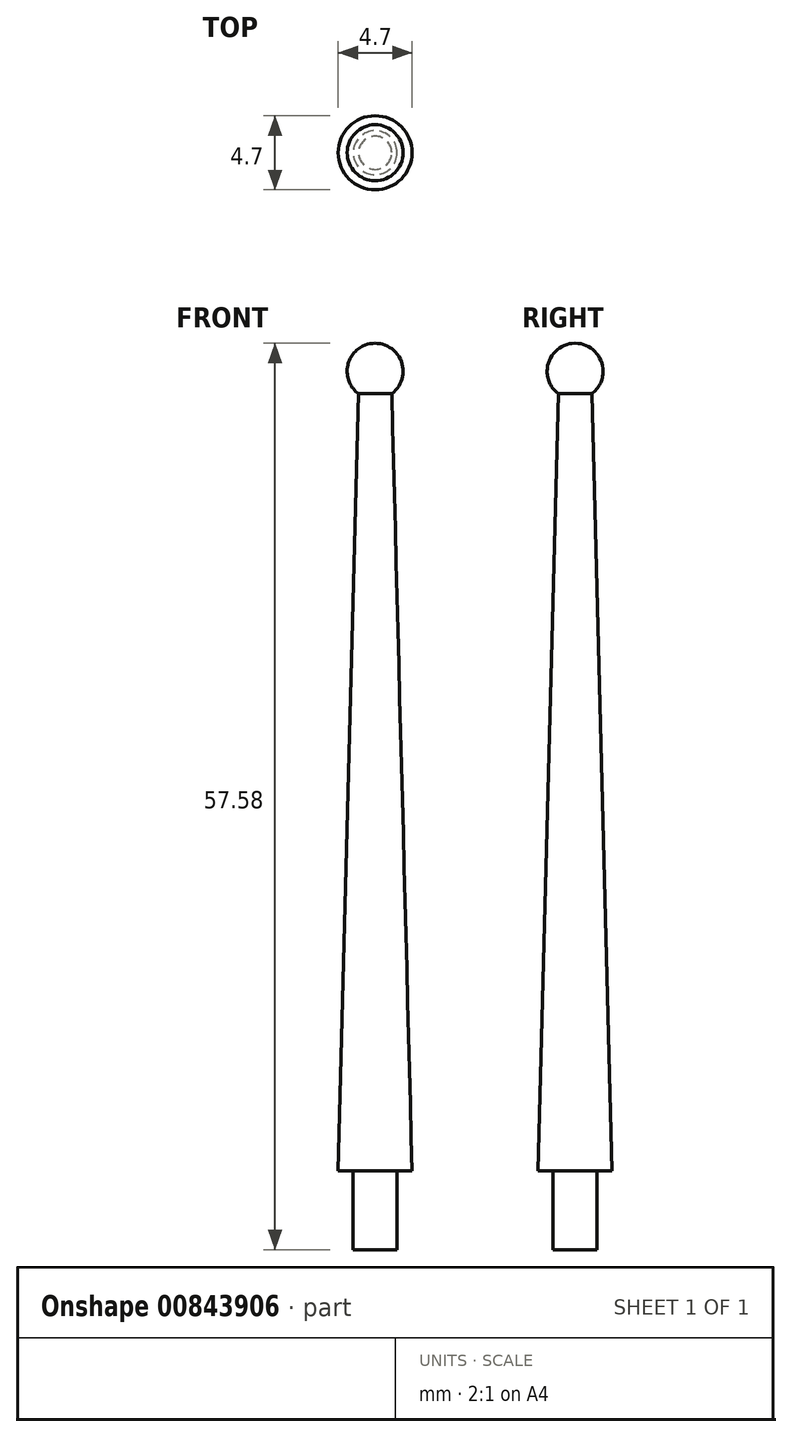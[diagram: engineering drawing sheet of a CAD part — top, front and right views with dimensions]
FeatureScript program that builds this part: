
annotation { "Feature Type Name" : "Feature", "Feature Type Description" : "" }
export const myFeature = defineFeature(function(context is Context, id is Id, definition is map)
    precondition{}
    {
        {
            var Q0;
            Q0=qCreatedBy(makeId("Top.planeOp"),FACE);
            var sketch = newSketch(context, id + "F0", { "sketchPlane" : qUnion([Q0])});
            skCircle(sketch, "E0", {"center": v(0, 0) * mm, "radius": 1.4 * mm});
            skSolve(sketch);
        }
        {
            var Q0;
            Q0 = qSketchRegion(id + "F0", true);
            extrude(context, id + "F1", {"entities" : qUnion([Q0]), "depth" : 5 * mm, "offsetDistance" : 25.4 * mm});
        }
        {
            var Q0;
            Q0=makeQuery(id+"F1.opExtrude","CAP_FACE",FACE,{"disambiguationData":[OSD([sQuery(id+"F0.wireOp",EDGE,"E0")])],"isStart":false});
            var sketch = newSketch(context, id + "F2", { "sketchPlane" : qUnion([Q0])});
            skCircle(sketch, "E1", {"center": v(0, 0) * mm, "radius": 2.35 * mm});
            skSolve(sketch);
        }
        {
            var Q0;
            Q0 = qSketchRegion(id + "F2", true);
            extrude(context, id + "F3", {"entities" : qUnion([Q0]), "operationType" : NewBodyOperationType.ADD, "depth" : 50.8 * mm, "offsetDistance" : 25.4 * mm, "hasDraft" : true, "draftAngle" : 1.5 * degree, "draftPullDirection" : true});
        }
        {
            var Q0;
            Q0=makeQuery(id+"F3.opExtrude","CAP_FACE",FACE,{"disambiguationData":[OSD([sQuery(id+"F2.wireOp",EDGE,"E1")])],"isStart":false});
            var sketch = newSketch(context, id + "F4", { "sketchPlane" : qUnion([Q0])});
            skArc(sketch, "E2", {"start": v(0, 1.78) * mm, "mid": v(-1.78, 0) * mm, "end": v(0, -1.78) * mm});
            skLineSegment(sketch, "E3", {"start": v(0, 1.78) * mm, "end": v(0, -1.78) * mm});
            skSolve(sketch);
        }
        {
            var Q0;
            Q0 = qSketchRegion(id + "F4", true);
            var Q1;
            Q1=sQuery(id+"F4.wireOp",EDGE,"E3");
            revolve(context, id + "F5", {"operationType" : NewBodyOperationType.ADD, "surfaceOperationType" : NewSurfaceOperationType.NEW, "entities" : qUnion([Q0]), "axis" : qUnion([Q1]), "revolveType" : RevolveType.FULL});
        }
    });
